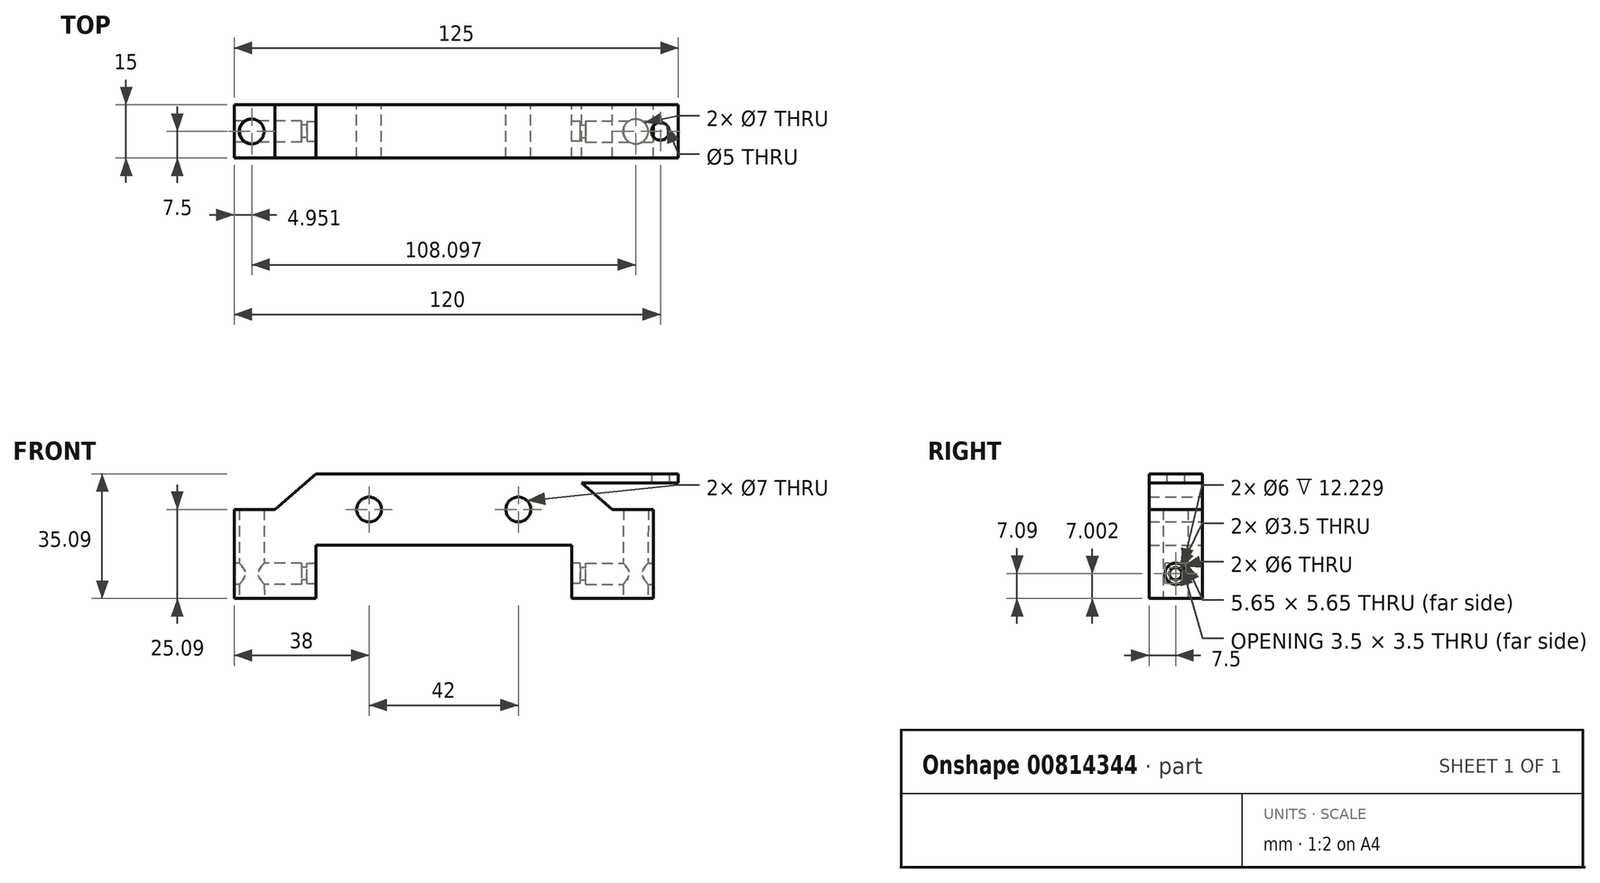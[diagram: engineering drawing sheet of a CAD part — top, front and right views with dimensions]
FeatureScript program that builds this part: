
annotation { "Feature Type Name" : "Feature", "Feature Type Description" : "" }
export const myFeature = defineFeature(function(context is Context, id is Id, definition is map)
    precondition{}
    {
        {
            var Q0;
            Q0=qCreatedBy(makeId("Front.planeOp"),FACE);
            var sketch = newSketch(context, id + "F0", { "sketchPlane" : qUnion([Q0])});
            skLineSegment(sketch, "E0.bottom", {"start": v(-36, 10) * mm, "end": v(36, 10) * mm});
            skLineSegment(sketch, "E0.top", {"start": v(-36, -10) * mm, "end": v(36, -10) * mm});
            skLineSegment(sketch, "E0.left", {"start": v(-36, 10) * mm, "end": v(-36, -10) * mm});
            skLineSegment(sketch, "E0.right", {"start": v(36, 10) * mm, "end": v(36, -10) * mm});
            skPoint(sketch, "E0.middle", {"position": v(0, 0) * mm});
            skLineSegment(sketch, "E1", {"start": v(36, 0) * mm, "end": v(21, 0) * mm});
            skCircle(sketch, "E2", {"center": v(21, 0) * mm, "radius": 3.5 * mm});
            skCircle(sketch, "E3.MirrorC", {"center": v(-21, 0) * mm, "radius": 3.5 * mm});
            skLineSegment(sketch, "E4", {"start": v(-36, -10) * mm, "end": v(-59, -10) * mm});
            skLineSegment(sketch, "E5", {"start": v(-59, -25.09) * mm, "end": v(-36, -25) * mm});
            skLineSegment(sketch, "E6", {"start": v(-36, -25) * mm, "end": v(-36, -10) * mm});
            skLineSegment(sketch, "E7", {"start": v(-59, -10) * mm, "end": v(-59, -25.09) * mm});
            skLineSegment(sketch, "E8.MirrorCS", {"start": v(59, -10) * mm, "end": v(59, -25.09) * mm});
            skLineSegment(sketch, "E9.MirrorCS", {"start": v(36, -25) * mm, "end": v(36, -10) * mm});
            skLineSegment(sketch, "E10.MirrorCS", {"start": v(59, -25.09) * mm, "end": v(36, -25) * mm});
            skLineSegment(sketch, "E11", {"start": v(36, 0) * mm, "end": v(59, 0) * mm});
            skLineSegment(sketch, "E12", {"start": v(59, 0) * mm, "end": v(59, -10) * mm});
            skLineSegment(sketch, "E13.MirrorCS", {"start": v(-36, 0) * mm, "end": v(-59, 0) * mm});
            skLineSegment(sketch, "E14.MirrorCS", {"start": v(-59, 0) * mm, "end": v(-59, -10) * mm});
            skLineSegment(sketch, "E15.bottom", {"start": v(36, 10) * mm, "end": v(66, 10) * mm});
            skLineSegment(sketch, "E15.top", {"start": v(36, 7.5) * mm, "end": v(66, 7.5) * mm});
            skLineSegment(sketch, "E15.left", {"start": v(36, 10) * mm, "end": v(36, 7.5) * mm});
            skLineSegment(sketch, "E15.right", {"start": v(66, 10) * mm, "end": v(66, 7.5) * mm});
            skLineSegment(sketch, "E16", {"start": v(-36, 10) * mm, "end": v(-47.5, 0) * mm});
            skLineSegment(sketch, "E17.MirrorCS", {"start": v(36, 10) * mm, "end": v(47.5, 0) * mm});
            skSolve(sketch);
        }
        {
            var Q0;
            Q0 = qSketchRegion(id + "F0", true);
            extrude(context, id + "F1", {"entities" : qUnion([Q0]), "depth" : 15 * mm, "offsetDistance" : 25 * mm});
        }
        {
            var Q0;
            Q0=makeQuery(id+"F1.opExtrude","SWEPT_FACE",FACE,{"disambiguationData":[OSD([sQuery(id+"F0.wireOp",EDGE,"E10.MirrorCS")])]});
            var sketch = newSketch(context, id + "F2", { "sketchPlane" : qUnion([Q0])});
            skLineSegment(sketch, "E18", {"start": v(59.1, 7.5) * mm, "end": v(54.1, 7.5) * mm});
            skCircle(sketch, "E19", {"center": v(54.1, 7.5) * mm, "radius": 3.5 * mm});
            skSolve(sketch);
        }
        {
            var Q0;
            Q0=makeQuery(id+"F1.opExtrude","SWEPT_FACE",FACE,{"disambiguationData":[OSD([sQuery(id+"F0.wireOp",EDGE,"E8.MirrorCS"),sQuery(id+"F0.wireOp",EDGE,"E12")])]});
            var sketch = newSketch(context, id + "F3", { "sketchPlane" : qUnion([Q0])});
            skLineSegment(sketch, "E20", {"start": v(-7.5, -25.09) * mm, "end": v(-7.5, -18.09) * mm});
            skCircle(sketch, "E21", {"center": v(-7.5, -18.09) * mm, "radius": 3 * mm});
            skCircle(sketch, "E22", {"center": v(-7.5, -18.09) * mm, "radius": 1.75 * mm});
            skSolve(sketch);
        }
        {
            var Q0;
            Q0=makeQuery(id+"F1.opExtrude","SWEPT_FACE",FACE,{"disambiguationData":[OSD([sQuery(id+"F0.wireOp",EDGE,"E9.MirrorCS")])]});
            var sketch = newSketch(context, id + "F4", { "sketchPlane" : qUnion([Q0])});
            skLineSegment(sketch, "E23", {"start": v(7.5, -25) * mm, "end": v(7.5, -18) * mm});
            skLineSegment(sketch, "E24.bottom", {"start": v(10.32, -20.82) * mm, "end": v(4.68, -20.82) * mm});
            skLineSegment(sketch, "E24.top", {"start": v(10.32, -15.17) * mm, "end": v(4.67, -15.17) * mm});
            skLineSegment(sketch, "E24.left", {"start": v(10.32, -20.82) * mm, "end": v(10.32, -15.17) * mm});
            skLineSegment(sketch, "E24.right", {"start": v(4.68, -20.82) * mm, "end": v(4.67, -15.17) * mm});
            skPoint(sketch, "E24.middle", {"position": v(7.5, -18) * mm});
            skSolve(sketch);
        }
        {
            var Q0;
            Q0=makeQuery(id+"F3.imprint","IMPRINT",FACE,{"disambiguationData":[TD([[makeQuery(id+"F3.imprint","IMPRINT",EDGE,{"derivedFrom":sQuery(id+"F3.wireOp",EDGE,"E22")}),1.0]])]});
            extrude(context, id + "F5", {"entities" : qUnion([Q0]), "operationType" : NewBodyOperationType.REMOVE, "oppositeDirection" : true, "depth" : 23 * mm, "offsetDistance" : 25 * mm});
        }
        {
            var Q0;
            Q0=makeQuery(id+"F3.imprint","IMPRINT",FACE,{"disambiguationData":[TD([[makeQuery(id+"F3.imprint","IMPRINT",EDGE,{"derivedFrom":sQuery(id+"F3.wireOp",EDGE,"E21")}),1.0]])]});
            extrude(context, id + "F6", {"entities" : qUnion([Q0]), "operationType" : NewBodyOperationType.REMOVE, "oppositeDirection" : true, "depth" : 19 * mm, "offsetDistance" : 25 * mm});
        }
        {
            var Q0;
            Q0=makeQuery(id+"F2.imprint","IMPRINT",FACE,{"disambiguationData":[TD([[makeQuery(id+"F2.imprint","IMPRINT",EDGE,{"derivedFrom":sQuery(id+"F2.wireOp",EDGE,"E19")}),1.0]])]});
            extrude(context, id + "F7", {"entities" : qUnion([Q0]), "operationType" : NewBodyOperationType.REMOVE, "oppositeDirection" : true, "depth" : 26 * mm, "offsetDistance" : 25 * mm});
        }
        {
            var Q0;
            Q0=makeQuery(id+"F4.imprint","IMPRINT",FACE,{"disambiguationData":[TD([[makeQuery(id+"F4.imprint","IMPRINT",EDGE,{"derivedFrom":sQuery(id+"F4.wireOp",EDGE,"E24.top")}),1.0]])]});
            extrude(context, id + "F8", {"entities" : qUnion([Q0]), "operationType" : NewBodyOperationType.REMOVE, "oppositeDirection" : true, "depth" : 2.5 * mm, "offsetDistance" : 25 * mm});
        }
        {
            var Q0;
            Q0=makeQuery(id+"F1.opExtrude","SWEPT_FACE",FACE,{"disambiguationData":[OSD([sQuery(id+"F0.wireOp",EDGE,"E7"),sQuery(id+"F0.wireOp",EDGE,"E14.MirrorCS")])]});
            var sketch = newSketch(context, id + "F9", { "sketchPlane" : qUnion([Q0])});
            skLineSegment(sketch, "E25", {"start": v(7.5, -25.09) * mm, "end": v(7.5, -18.09) * mm});
            skCircle(sketch, "E26", {"center": v(7.5, -18.09) * mm, "radius": 1.75 * mm});
            skCircle(sketch, "E27", {"center": v(7.5, -18.09) * mm, "radius": 3 * mm});
            skSolve(sketch);
        }
        {
            var Q0;
            Q0=makeQuery(id+"F1.opExtrude","SWEPT_FACE",FACE,{"disambiguationData":[OSD([sQuery(id+"F0.wireOp",EDGE,"E6")])]});
            var sketch = newSketch(context, id + "F10", { "sketchPlane" : qUnion([Q0])});
            skLineSegment(sketch, "E28", {"start": v(-7.5, -25) * mm, "end": v(-7.5, -18) * mm});
            skLineSegment(sketch, "E29.bottom", {"start": v(-4.68, -20.82) * mm, "end": v(-10.33, -20.82) * mm});
            skLineSegment(sketch, "E29.top", {"start": v(-4.67, -15.17) * mm, "end": v(-10.32, -15.17) * mm});
            skLineSegment(sketch, "E29.left", {"start": v(-4.67, -20.82) * mm, "end": v(-4.67, -15.17) * mm});
            skLineSegment(sketch, "E29.right", {"start": v(-10.33, -20.82) * mm, "end": v(-10.32, -15.17) * mm});
            skPoint(sketch, "E29.middle", {"position": v(-7.5, -18) * mm});
            skSolve(sketch);
        }
        {
            var Q0;
            Q0=makeQuery(id+"F1.opExtrude","SWEPT_FACE",FACE,{"disambiguationData":[OSD([sQuery(id+"F0.wireOp",EDGE,"E5")])]});
            var sketch = newSketch(context, id + "F11", { "sketchPlane" : qUnion([Q0])});
            skLineSegment(sketch, "E30", {"start": v(-59.1, 7.5) * mm, "end": v(-54.1, 7.5) * mm});
            skCircle(sketch, "E31", {"center": v(-54.1, 7.5) * mm, "radius": 3.5 * mm});
            skSolve(sketch);
        }
        {
            var Q0;
            Q0=makeQuery(id+"F9.imprint","IMPRINT",FACE,{"disambiguationData":[TD([[makeQuery(id+"F9.imprint","IMPRINT",EDGE,{"derivedFrom":sQuery(id+"F9.wireOp",EDGE,"E26")}),-1.0]])]});
            extrude(context, id + "F12", {"entities" : qUnion([Q0]), "operationType" : NewBodyOperationType.REMOVE, "oppositeDirection" : true, "depth" : 19 * mm, "offsetDistance" : 25 * mm});
        }
        {
            var Q0;
            Q0=makeQuery(id+"F9.imprint","IMPRINT",FACE,{"disambiguationData":[TD([[makeQuery(id+"F9.imprint","IMPRINT",EDGE,{"derivedFrom":sQuery(id+"F9.wireOp",EDGE,"E26")}),1.0]])]});
            extrude(context, id + "F13", {"entities" : qUnion([Q0]), "operationType" : NewBodyOperationType.REMOVE, "oppositeDirection" : true, "depth" : 23 * mm, "offsetDistance" : 25 * mm});
        }
        {
            var Q0;
            Q0=makeQuery(id+"F10.imprint","IMPRINT",FACE,{"disambiguationData":[TD([[makeQuery(id+"F10.imprint","IMPRINT",EDGE,{"derivedFrom":sQuery(id+"F10.wireOp",EDGE,"E29.top")}),1.0]])]});
            extrude(context, id + "F14", {"entities" : qUnion([Q0]), "operationType" : NewBodyOperationType.REMOVE, "oppositeDirection" : true, "depth" : 2.5 * mm, "offsetDistance" : 25 * mm});
        }
        {
            var Q0;
            Q0=makeQuery(id+"F11.imprint","IMPRINT",FACE,{"disambiguationData":[TD([[makeQuery(id+"F11.imprint","IMPRINT",EDGE,{"derivedFrom":sQuery(id+"F11.wireOp",EDGE,"E31")}),1.0]])]});
            extrude(context, id + "F15", {"entities" : qUnion([Q0]), "operationType" : NewBodyOperationType.REMOVE, "oppositeDirection" : true, "depth" : 25.1 * mm, "offsetDistance" : 25 * mm});
        }
        {
            var Q0;
            Q0=makeQuery(id+"F1.opExtrude","SWEPT_FACE",FACE,{"disambiguationData":[OSD([sQuery(id+"F0.wireOp",EDGE,"E15.top")])]});
            var sketch = newSketch(context, id + "F16", { "sketchPlane" : qUnion([Q0])});
            skLineSegment(sketch, "E32", {"start": v(66, 7.5) * mm, "end": v(61, 7.5) * mm});
            skCircle(sketch, "E33", {"center": v(61, 7.5) * mm, "radius": 2.5 * mm});
            skSolve(sketch);
        }
        {
            var Q0;
            Q0 = qSketchRegion(id + "F16", true);
            extrude(context, id + "F17", {"entities" : qUnion([Q0]), "operationType" : NewBodyOperationType.REMOVE, "oppositeDirection" : true, "depth" : 25 * mm, "offsetDistance" : 25 * mm});
        }
    });
